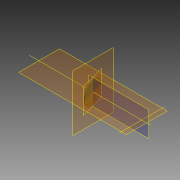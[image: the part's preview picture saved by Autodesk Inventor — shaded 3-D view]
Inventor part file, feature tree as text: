
AUTODESK INVENTOR PART (.ipt)
format: ipt  version: 2015 (Build 190159000, 159)  size: 126,976 bytes
history: native  units: mm
features: sketch x4, extrude x3, plane x2, other x1, hole x1
ambient origin geometry x8: Origin, YZ Plane, XZ Plane, XY Plane, X Axis, Y Axis, Z Axis, Center Point
bodies: Solid1 (feature_tree)
feature tree (11):
  plane  "Work Plane1"
  extrude  "Extrusion1"  Depth=1.0mm TaperAngle=0.0deg
  plane  "Work Plane2"
  extrude  "Extrusion2"  Depth=35.0mm
  other  "Work Axis1"
  extrude  "Extrusion4"  TaperAngle=15.0deg  [1 undecoded]
  hole  "Hole2"  [1 undecoded]
  sketch  "Sketch1"  dims[d2=1.0mm d3=30.0mm d4=30.0mm d5=0.0mm d6=0.0mm]
  sketch  "Sketch2"  dims[d7=30.0mm d8=0.0mm d26=35.0mm]
  sketch  "Sketch5"  dims[d28=17.664158mm d29=15.0deg]
  sketch  "Sketch7"  dims[d30=28.0mm d31=10.0mm d32=0.0mm d34=3.0mm d35=7.5mm d36=7.5mm d37=3.0mm d38=6.0mm d39=4.0mm d40=2.0mm d41=90.0deg d42=8.0mm d43=20.594885mm]
note: 2 required parameter values undecoded (feature->parameter linkage not recoverable at this tier; creation-order binding heuristic only, values carry confidence <= 0.55)
